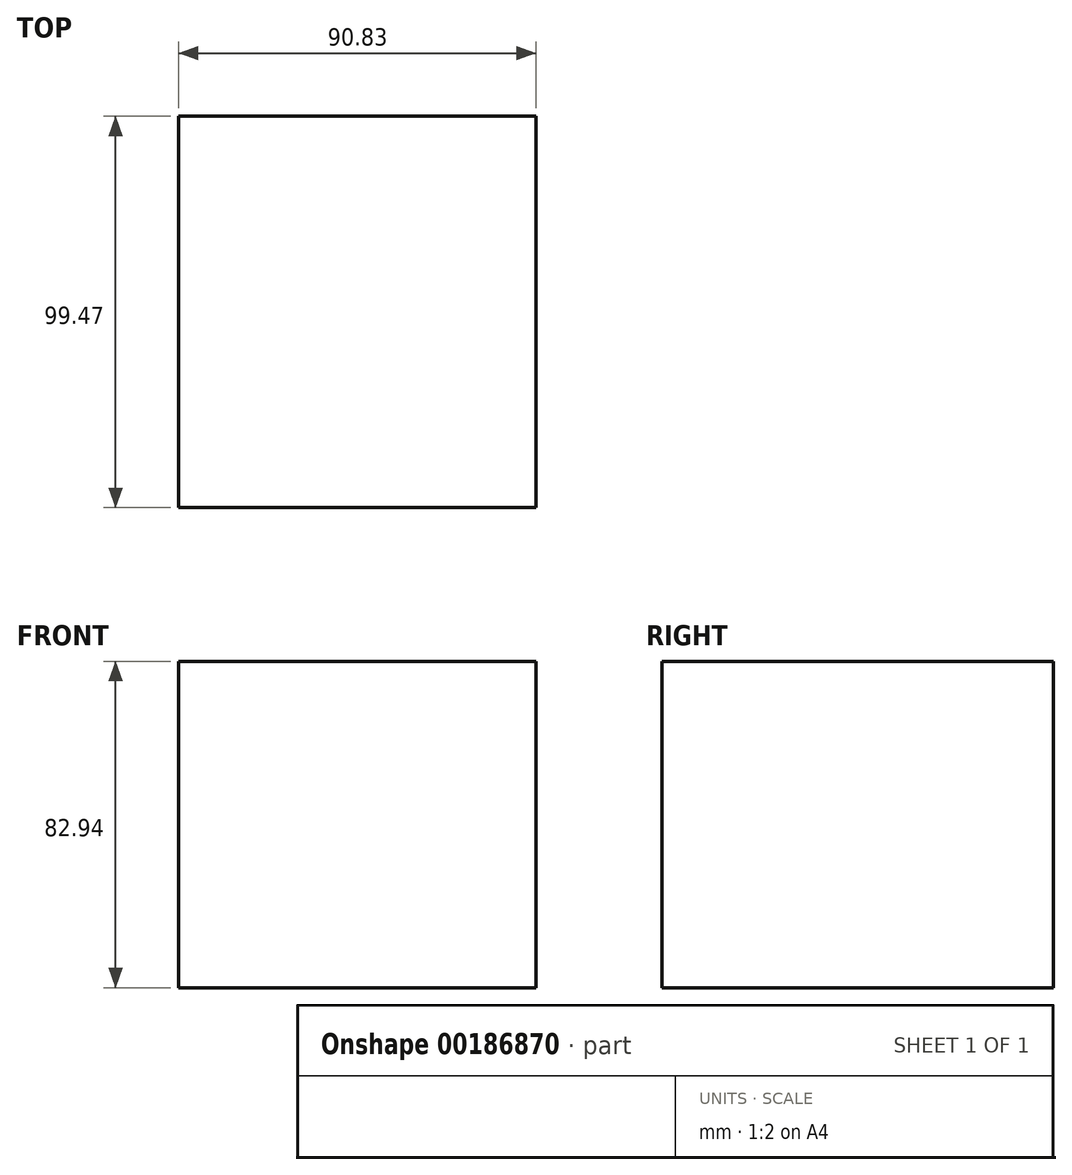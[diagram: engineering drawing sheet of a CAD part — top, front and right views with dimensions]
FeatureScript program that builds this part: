
annotation { "Feature Type Name" : "Feature", "Feature Type Description" : "" }
export const myFeature = defineFeature(function(context is Context, id is Id, definition is map)
    precondition{}
    {
        {
            var Q0;
            Q0=qCreatedBy(makeId("Top.planeOp"),FACE);
            var sketch = newSketch(context, id + "F0", { "sketchPlane" : qUnion([Q0])});
            skLineSegment(sketch, "E0.bottom", {"start": v(-48.77, -42.84) * mm, "end": v(42.06, -42.84) * mm});
            skLineSegment(sketch, "E0.top", {"start": v(-48.77, 56.63) * mm, "end": v(42.06, 56.63) * mm});
            skLineSegment(sketch, "E0.left", {"start": v(-48.77, -42.84) * mm, "end": v(-48.77, 56.63) * mm});
            skLineSegment(sketch, "E0.right", {"start": v(42.06, -42.84) * mm, "end": v(42.06, 56.63) * mm});
            skSolve(sketch);
        }
        {
            var Q0;
            Q0 = qSketchRegion(id + "F0", true);
            extrude(context, id + "F1", {"entities" : qUnion([Q0]), "depth" : 82.94 * mm});
        }
    });
